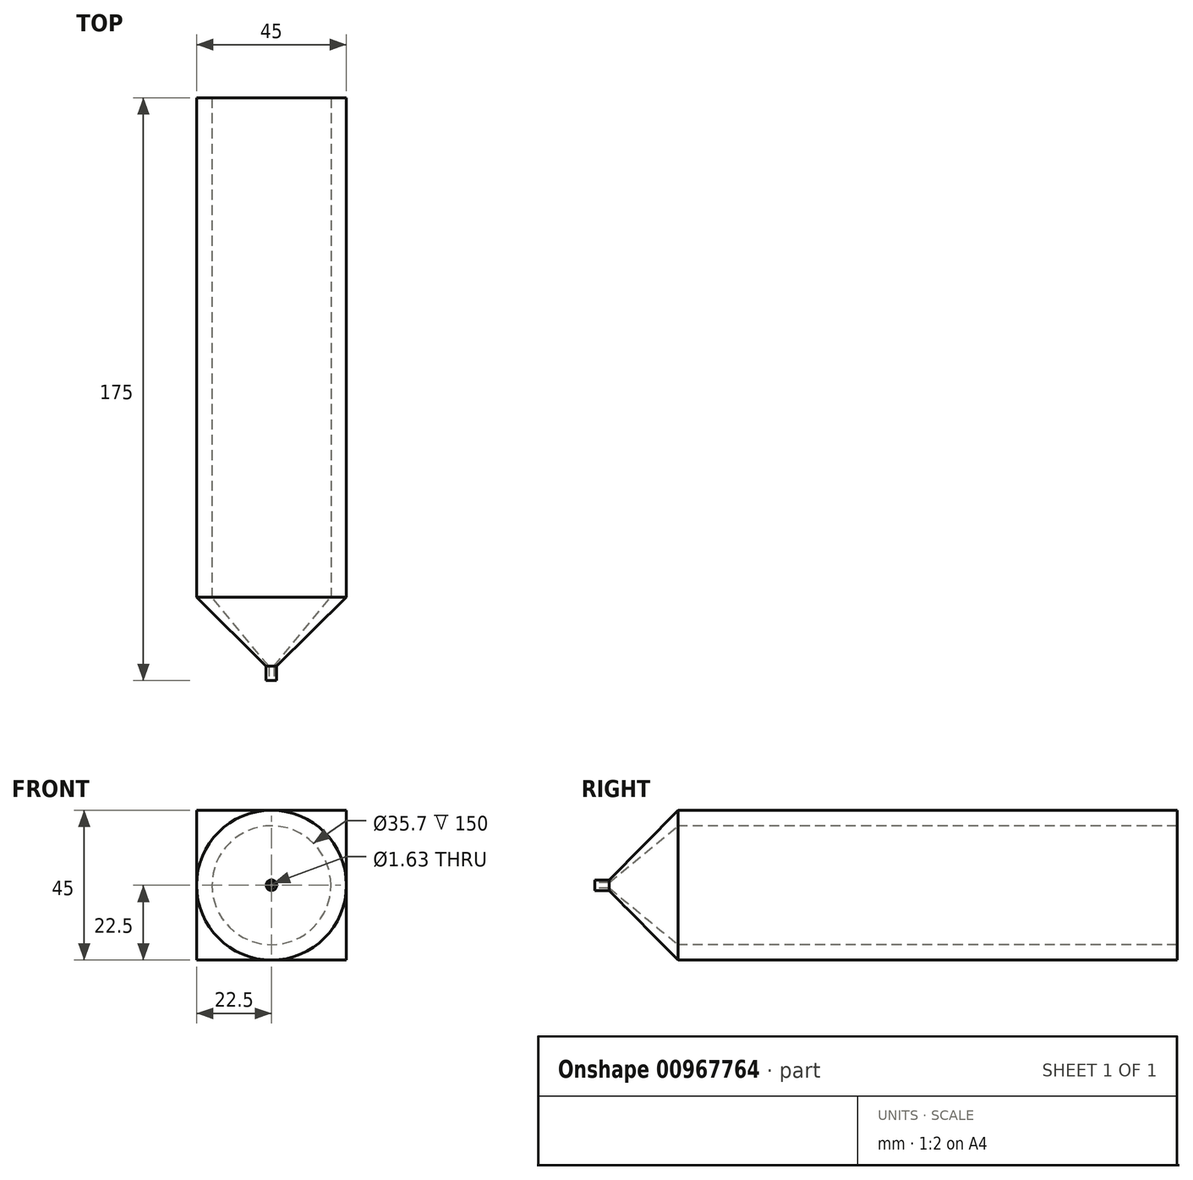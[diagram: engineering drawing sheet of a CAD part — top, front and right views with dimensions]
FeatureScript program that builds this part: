
annotation { "Feature Type Name" : "Feature", "Feature Type Description" : "" }
export const myFeature = defineFeature(function(context is Context, id is Id, definition is map)
    precondition{}
    {
        {
            var Q0;
            Q0=qCreatedBy(makeId("Front.planeOp"),FACE);
            var sketch = newSketch(context, id + "F0", { "sketchPlane" : qUnion([Q0])});
            skCircle(sketch, "E0", {"center": v(0, 0) * mm, "radius": 17.85 * mm});
            skLineSegment(sketch, "E1.bottom", {"start": v(22.5, -22.5) * mm, "end": v(-22.5, -22.5) * mm});
            skLineSegment(sketch, "E1.top", {"start": v(22.5, 22.5) * mm, "end": v(-22.5, 22.5) * mm});
            skLineSegment(sketch, "E1.left", {"start": v(22.5, -22.5) * mm, "end": v(22.5, 22.5) * mm});
            skLineSegment(sketch, "E1.right", {"start": v(-22.5, -22.5) * mm, "end": v(-22.5, 22.5) * mm});
            skCircle(sketch, "E2", {"center": v(0, 0) * mm, "radius": 1.59 * mm});
            skCircle(sketch, "E3", {"center": v(0, 0) * mm, "radius": 0.81 * mm});
            skSolve(sketch);
        }
        {
            var Q0;
            Q0 = qSketchRegion(id + "F0", true);
            extrude(context, id + "F1", {"entities" : qUnion([Q0]), "oppositeDirection" : true, "depth" : 150 * mm, "offsetDistance" : 25 * mm});
        }
        {
            var Q0;
            Q0=makeQuery(id+"F0.imprint","IMPRINT",FACE,{"disambiguationData":[TD([[makeQuery(id+"F0.imprint","IMPRINT",EDGE,{"derivedFrom":sQuery(id+"F0.wireOp",EDGE,"E0")}),-1.0]])]});
            cPlane(context, id + "F2", {"entities" : qUnion([Q0]), "cplaneType" : CPlaneType.OFFSET, "offset" : 25 * mm, "width" : 150 * mm, "height" : 150 * mm});
        }
        {
            var Q0;
            Q0=qCreatedBy(id+"F2.planeOp",FACE);
            var sketch = newSketch(context, id + "F3", { "sketchPlane" : qUnion([Q0])});
            skCircle(sketch, "E4.0", {"center": v(0, 0) * mm, "radius": 0.81 * mm});
            skCircle(sketch, "E5.0", {"center": v(0, 0) * mm, "radius": 1.59 * mm});
            skSolve(sketch);
        }
        {
            var Q0;
            Q0 = qSketchRegion(id + "F3", true);
            extrude(context, id + "F4", {"entities" : qUnion([Q0]), "oppositeDirection" : true, "depth" : 4.3 * mm, "offsetDistance" : 25 * mm});
        }
        {
            var Q0;
            Q0=qCreatedBy(makeId("Right.planeOp"),FACE);
            var sketch = newSketch(context, id + "F5", { "sketchPlane" : qUnion([Q0])});
            skLineSegment(sketch, "E6.0.0", {"start": v(0, -22.5) * mm, "end": v(0, 22.5) * mm});
            skLineSegment(sketch, "E6.0.1", {"start": v(0, 22.5) * mm, "end": v(150, 22.5) * mm});
            skLineSegment(sketch, "E6.0.2", {"start": v(150, 22.5) * mm, "end": v(150, -22.5) * mm});
            skLineSegment(sketch, "E6.0.3", {"start": v(150, -22.5) * mm, "end": v(0, -22.5) * mm});
            skLineSegment(sketch, "E7", {"start": v(-25, 1.59) * mm, "end": v(-20.7, 1.59) * mm});
            skLineSegment(sketch, "E8", {"start": v(-20.7, -1.59) * mm, "end": v(-25, -1.59) * mm});
            skLineSegment(sketch, "E9", {"start": v(-20.7, 1.59) * mm, "end": v(0, 22.5) * mm});
            skLineSegment(sketch, "E10", {"start": v(0, -22.5) * mm, "end": v(-20.7, -1.59) * mm});
            skLineSegment(sketch, "E11.0", {"start": v(-20.7, -1.59) * mm, "end": v(-20.7, 1.59) * mm});
            skLineSegment(sketch, "E12.0", {"start": v(-20.7, -0.81) * mm, "end": v(-20.7, 0.81) * mm});
            skLineSegment(sketch, "E13.0.2", {"start": v(0, 22.5) * mm, "end": v(0, -22.5) * mm});
            skLineSegment(sketch, "E14.0.0", {"start": v(0, -17.85) * mm, "end": v(0, 17.85) * mm});
            skLineSegment(sketch, "E15", {"start": v(0, 17.85) * mm, "end": v(-20.7, 0.81) * mm});
            skLineSegment(sketch, "E16", {"start": v(-20.7, -0.81) * mm, "end": v(0, -17.85) * mm});
            skLineSegment(sketch, "E17", {"start": v(0, 0) * mm, "end": v(45.63, 0) * mm});
            skSolve(sketch);
        }
        {
            var Q0;
            {var subQ0=sQuery(id+"F5.wireOp",EDGE,"E9");Q0=makeQuery(id+"F5.imprint","IMPRINT",FACE,{"disambiguationData":[TD([[makeQuery(id+"F5.imprint","IMPRINT",EDGE,{"derivedFrom":subQ0}),-1.0]])]});}
            var Q1;
            Q1=sQuery(id+"F5.wireOp",EDGE,"E17");
            revolve(context, id + "F6", {"operationType" : NewBodyOperationType.ADD, "surfaceOperationType" : NewSurfaceOperationType.NEW, "entities" : qUnion([Q0]), "axis" : qUnion([Q1]), "revolveType" : RevolveType.FULL});
        }
    });
